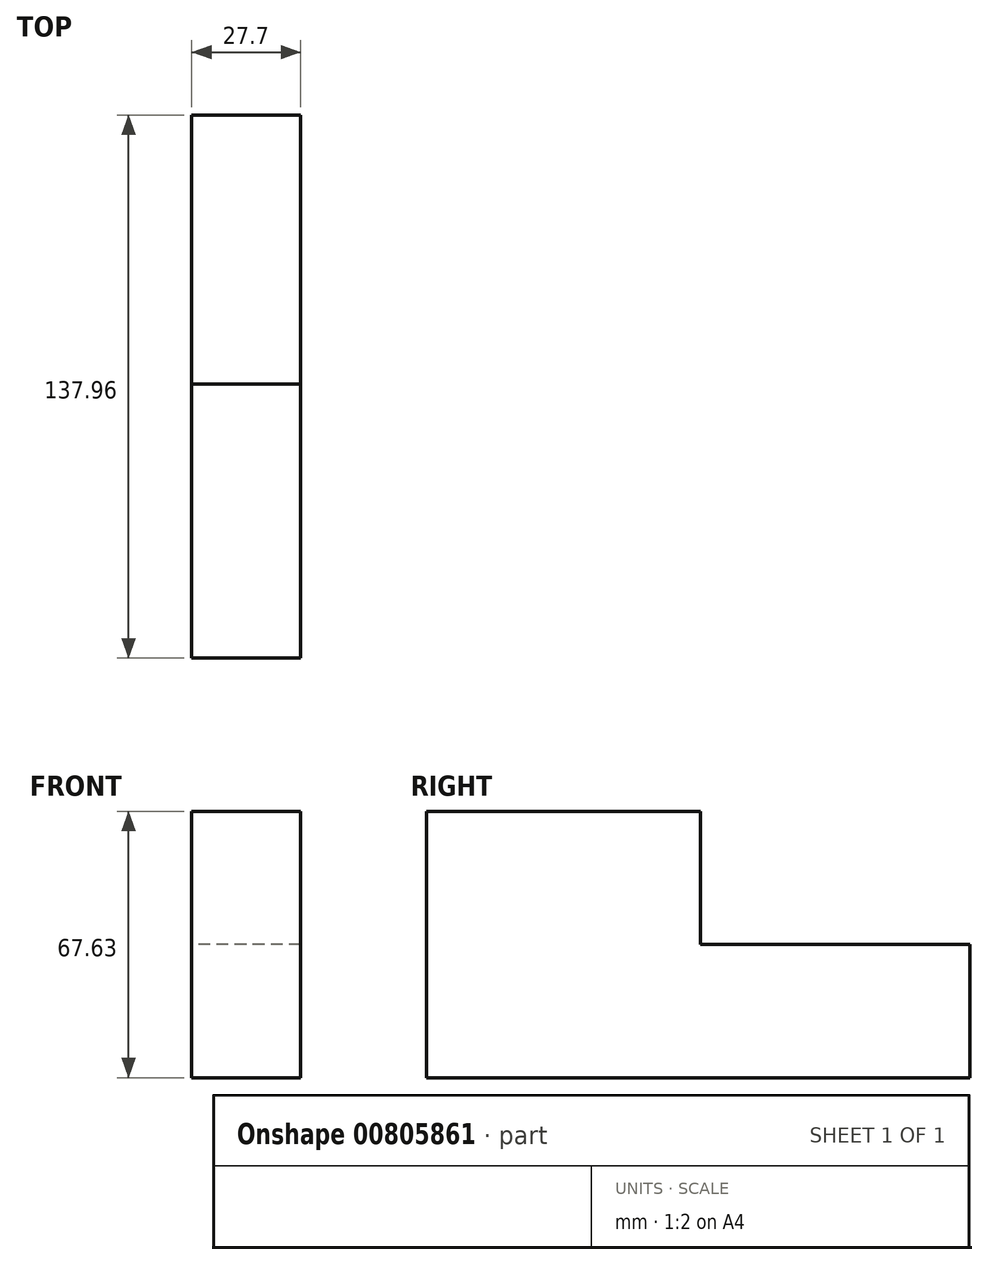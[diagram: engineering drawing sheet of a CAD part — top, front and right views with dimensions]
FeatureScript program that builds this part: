
annotation { "Feature Type Name" : "Feature", "Feature Type Description" : "" }
export const myFeature = defineFeature(function(context is Context, id is Id, definition is map)
    precondition{}
    {
        {
            var Q0;
            Q0=qCreatedBy(makeId("Right.planeOp"),FACE);
            var sketch = newSketch(context, id + "F0", { "sketchPlane" : qUnion([Q0])});
            skLineSegment(sketch, "E0.bottom", {"start": v(68.38, 23) * mm, "end": v(-69.58, 23) * mm});
            skLineSegment(sketch, "E0.top", {"start": v(68.38, -44.64) * mm, "end": v(-69.58, -44.64) * mm});
            skLineSegment(sketch, "E0.left", {"start": v(68.38, 23) * mm, "end": v(68.38, -44.64) * mm});
            skLineSegment(sketch, "E0.right", {"start": v(-69.58, 23) * mm, "end": v(-69.58, -44.64) * mm});
            skSolve(sketch);
        }
        {
            var Q0;
            Q0=makeQuery(id+"F0.imprint","IMPRINT",FACE,{"disambiguationData":[TD([[makeQuery(id+"F0.imprint","IMPRINT",EDGE,{"derivedFrom":sQuery(id+"F0.wireOp",EDGE,"E0.bottom")}),1.0]])]});
            extrude(context, id + "F1", {"entities" : qUnion([Q0]), "oppositeDirection" : true, "depth" : 27.7 * mm, "offsetDistance" : 25 * mm});
        }
        {
            var Q0;
            Q0=makeQuery(id+"F1.opExtrude","CAP_FACE",FACE,{"disambiguationData":[OSD([sQuery(id+"F0.wireOp",EDGE,"E0.bottom"),sQuery(id+"F0.wireOp",EDGE,"E0.top"),sQuery(id+"F0.wireOp",EDGE,"E0.left"),sQuery(id+"F0.wireOp",EDGE,"E0.right")])],"isStart":false});
            var sketch = newSketch(context, id + "F2", { "sketchPlane" : qUnion([Q0])});
            skLineSegment(sketch, "E1", {"start": v(-68.38, -10.82) * mm, "end": v(0, -10.82) * mm});
            skLineSegment(sketch, "E2", {"start": v(0, -10.82) * mm, "end": v(0, 23) * mm});
            skSolve(sketch);
        }
        {
            var Q0;
            {var subQ0=sQuery(id+"F2.wireOp",EDGE,"E1");Q0=makeQuery(id+"F2.imprint","IMPRINT",FACE,{"disambiguationData":[TD([[makeQuery(id+"F2.imprint","IMPRINT",EDGE,{"derivedFrom":subQ0}),1.0]])]});}
            extrude(context, id + "F3", {"entities" : qUnion([Q0]), "operationType" : NewBodyOperationType.REMOVE, "oppositeDirection" : true, "depth" : 36.4 * mm, "offsetDistance" : 25 * mm});
        }
    });
